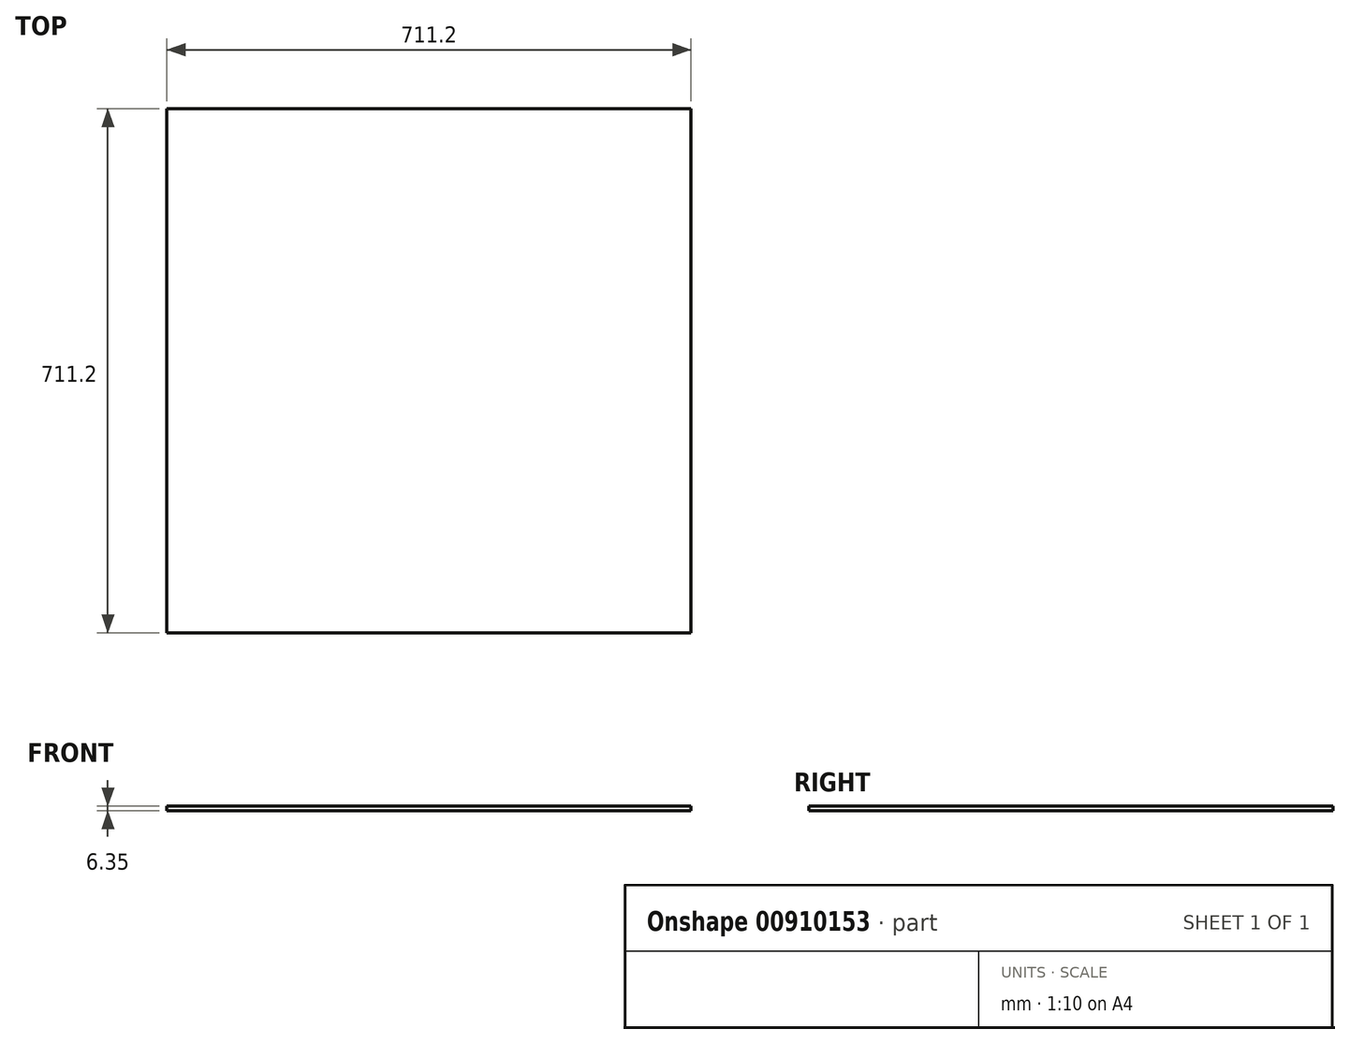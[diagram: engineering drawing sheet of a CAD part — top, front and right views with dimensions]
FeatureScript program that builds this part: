
annotation { "Feature Type Name" : "Feature", "Feature Type Description" : "" }
export const myFeature = defineFeature(function(context is Context, id is Id, definition is map)
    precondition{}
    {
        {
            var Q0;
            Q0=qCreatedBy(makeId("Top.planeOp"),FACE);
            var sketch = newSketch(context, id + "F0", { "sketchPlane" : qUnion([Q0])});
            skLineSegment(sketch, "E0.bottom", {"start": v(0, 0) * mm, "end": v(711.2, 0) * mm});
            skLineSegment(sketch, "E0.top", {"start": v(0, 711.2) * mm, "end": v(711.2, 711.2) * mm});
            skLineSegment(sketch, "E0.left", {"start": v(0, 0) * mm, "end": v(0, 711.2) * mm});
            skLineSegment(sketch, "E0.right", {"start": v(711.2, 0) * mm, "end": v(711.2, 711.2) * mm});
            skSolve(sketch);
        }
        {
            var Q0;
            Q0=makeQuery(id+"F0.imprint","IMPRINT",FACE,{"disambiguationData":[TD([[makeQuery(id+"F0.imprint","IMPRINT",EDGE,{"derivedFrom":sQuery(id+"F0.wireOp",EDGE,"E0.bottom")}),1.0]])]});
            extrude(context, id + "F1", {"entities" : qUnion([Q0]), "depth" : 6.35 * mm, "offsetDistance" : 25.4 * mm});
        }
    });
